# Revit family: ef_eg-20_40ysxc2_a(t)sxc2_b(t)sxc2_d(t)sxc2_csxc2_60Hz
name_source: partatom
category: 機械設備
units: mm (PartAtom-declared; Revit-internal decimal feet)

## family parameters
OmniClass タイトル = Industrial Ventilating Equipment
OmniClass 番号 = 23.75.35.21.17
パーツ タイプ = 標準
ロード時にボイドで切り取り = はい
丸型コネクタ寸法 = 直径を使用
作業面ベース = いいえ
共有 = いいえ
常に垂直 = はい
部屋計算ポイント = はい

## types (11) — shared parameters
IfcExportAs = IfcFanType
IfcExportType = TUBEAXIAL
MID風量 = 0.0 m³/h
MIN風量 = 0.0 m³/h
OmniClassCode = 23-33 31 19 11 17
URL = https://www.mitsubishielectric.co.jp
Uniclass2015Code = Pr_65_67_29_67
Uniclass2015Title = Propeller fans
Uniclass2015Version = Systems v1.9
オリフィス_Depth = 45
ファンの種類 = 軸流羽根
フレームの厚さ = 10  [stored 0.0328084 ft]
レグ_Height = 413
レグ_Width = 413
仕様書バージョン = Version1.0
企業コード = 108420
分類コード = 50052503100110
周波数 = 60 Hz
呼称 = 有圧扇
法定耐用年数 = 15
製品リリース年月 = 2022年6月1日
製品出荷対象 = 国内
製造元 = 三菱電機株式会社
設置方法 = 壁付
説明 = 産業用有圧換気扇 低騒音形ステンレスタイプ オールステンレスタイプ 排気専用
負荷分類 = 3_ファン類
運転質量 = 0.00 kg

## per-type parameters (varying)
| type | Box_H | Box_W | Depth | Height | MAX風量 | Width | オリフィス径 | ボックス_Depth | ボックス_Height | ボックス_Width | モデル | モーター径 | レグ_Depth | 価格 | 極 | 極数 | 消費電力 | 相 | 羽根径 | 製品質量 | 質量 | 電動機出力 | 電圧 |
| EF-20YSXC2 | 84 | 117 | 164  [stored 0.538058 ft] | 320  [stored 1.04987 ft] | 780.0 m³/h | 320  [stored 1.04987 ft] | 257  [stored 0.843176 ft] | 40 | 103 | 38 | EF-20YSXC2 | 99  [stored 0.324803 ft] | 148 | 136000 $ | 4 | 2 | 28 W | 1 | ∅200 | 3.60 kg | 4.32 kg | 15 W | 100 V |
| EF-25ASXC2 | 83 | 137 | 164  [stored 0.538058 ft] | 370 | 1260.0 m³/h | 370 | 298 | 45 | 131  [stored 0.42979 ft] | 46 | EF-25ASXC2 | 99  [stored 0.324803 ft] | 148 | 139000 $ | 4 | 2 | 49 W | 1 | ∅250 | 4.40 kg | 5.28 kg | 25 W | 100 V |
| EF-30BSXC2 | 108 | 162 | 164  [stored 0.538058 ft] | 420 | 1980.0 m³/h | 420 | 348 | 45 | 131  [stored 0.42979 ft] | 46 | EF-30BSXC2 | 99  [stored 0.324803 ft] | 148 | 188000 $ | 4 | 2 | 73 W | 1 | ∅300 | 5.40 kg | 6.48 kg | 50 W | 100 V |
| EF-40DSXC2 | 185 | 213 | 225 | 520 | 4360.0 m³/h | 520 | 476 | 58 | 131  [stored 0.42979 ft] | 47 | EF-40DSXC2 | 113 | 199 | 234000 $ | 4 | 2 | 190 W | 1 | ∅400 | 12.50 kg | 15.00 kg | 200 W | 100 V |
| EG-40CSXC2 | 185 | 213 | 249 | 520 | 3660.0 m³/h | 520 | 476 | 58 | 131  [stored 0.42979 ft] | 47 | EG-40CSXC2 | 113 | 213 | 223000 $ | 6 | 2 | 118 W | 1 | ∅400 | 12.50 kg | 15.00 kg | 100 W | 100 V |
| EF-25ATXC2_200V | 83 | 137 | 164  [stored 0.538058 ft] | 370 | 1260.0 m³/h | 370 | 298 | 45 | 131  [stored 0.42979 ft] | 46 | EF-25ATXC2 | 99  [stored 0.324803 ft] | 148 | 139000 $ | 4 | 3 | 40 W | 3 | ∅250 | 4.80 kg | 5.76 kg | 25 W | 200 V |
| EF-30BTXC2_200V | 108 | 162 | 164  [stored 0.538058 ft] | 420 | 1980.0 m³/h | 420 | 348 | 45 | 131  [stored 0.42979 ft] | 46 | EF-30BTXC2 | 99  [stored 0.324803 ft] | 148 | 188000 $ | 4 | 3 | 65 W | 3 | ∅300 | 5.50 kg | 6.60 kg | 50 W | 200 V |
| EF-40DTXC2_200V | 185 | 213 | 225 | 520 | 4360.0 m³/h | 520 | 476 | 58 | 131  [stored 0.42979 ft] | 47 | EF-40DTXC2 | 113 | 199 | 234000 $ | 4 | 3 | 175 W | 3 | ∅400 | 12.50 kg | 15.00 kg | 200 W | 200 V |
| EF-25ATXC2_220V | 83 | 137 | 164  [stored 0.538058 ft] | 370 | 1260.0 m³/h | 370 | 298 | 45 | 131  [stored 0.42979 ft] | 46 | EF-25ATXC2 | 99  [stored 0.324803 ft] | 148 | 139000 $ | 4 | 3 | 42 W | 3 | ∅250 | 4.80 kg | 5.76 kg | 25 W | 220 V |
| EF-30BTXC2_220V | 108 | 162 | 164  [stored 0.538058 ft] | 420 | 1980.0 m³/h | 420 | 348 | 45 | 131  [stored 0.42979 ft] | 46 | EF-30BTXC2 | 99  [stored 0.324803 ft] | 148 | 188000 $ | 4 | 3 | 72 W | 3 | ∅300 | 5.50 kg | 6.60 kg | 50 W | 220 V |
| EF-40DTXC2_220V | 185 | 213 | 225 | 520 | 4360.0 m³/h | 520 | 476 | 58 | 131  [stored 0.42979 ft] | 47 | EF-40DTXC2 | 113 | 199 | 234000 $ | 4 | 3 | 190 W | 3 | ∅400 | 12.50 kg | 15.00 kg | 200 W | 220 V |

note: [stored X ft] marks values corroborated as IEEE doubles in the binary element streams (Revit-internal decimal feet)
